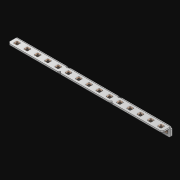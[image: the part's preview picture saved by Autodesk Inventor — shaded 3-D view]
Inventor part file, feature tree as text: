
AUTODESK INVENTOR PART (.ipt)
format: ipt  version: 2021 (Build 250183000, 183)  size: 669,696 bytes
history: native  units: in
note: dims shown in document units (in); Inventor stores cm internally (conversion verified against a paired STEP export)
features: extrude x31, other x30, sketch x3, pattern_linear x1, sheet_metal_op x1
ambient origin geometry x8: Origin, YZ Plane, XZ Plane, XY Plane, X Axis, Y Axis, Z Axis, Center Point
bodies: Solid1 (feature_tree)
feature tree (66):
  pattern_linear  "Rectangular Pattern1"  Spacing1=0.063in  [1 undecoded]
  extrude  "Extrusion1"  Depth=0.5in
  sketch  "Sketch1"  dims[d0=0.182in]
  other  "Srf1"
  sketch  "Sketch2"  dims[d1=0.063in d2=0.0in]
  other  "Srf2"
  other  "Srf3"
  other  "Srf5"
  other  "Srf7"
  other  "Srf9"
  other  "Srf11"
  other  "Srf13"
  other  "Srf15"
  other  "Srf17"
  other  "Srf19"
  other  "Srf21"
  other  "Srf23"
  other  "Srf25"
  other  "Srf27"
  other  "Srf29"
  other  "Srf4"
  other  "Srf6"
  other  "Srf8"
  other  "Srf10"
  other  "Srf12"
  other  "Srf14"
  other  "Srf16"
  other  "Srf18"
  other  "Srf20"
  other  "Srf22"
  other  "Srf24"
  other  "Srf26"
  other  "Srf28"
  other  "Srf30"
  sketch  "Sketch3"  dims[d3=0.182in d4=0.063in d5=0.0in d8=0.5in d9=10.0in d10=0.0in]
  sheet_metal_op  "Fold1"
  extrude  "ExtrusionSrf1"  Depth=0.5in TaperAngle=0.0deg
  extrude  "ExtrusionSrf2"  [1 undecoded]
  extrude  "ExtrusionSrf3"  [1 undecoded]
  extrude  "ExtrusionSrf4"  [1 undecoded]
  extrude  "ExtrusionSrf5"  [1 undecoded]
  extrude  "ExtrusionSrf6"  [1 undecoded]
  extrude  "ExtrusionSrf7"  [1 undecoded]
  extrude  "ExtrusionSrf8"  [1 undecoded]
  extrude  "ExtrusionSrf9"  [1 undecoded]
  extrude  "ExtrusionSrf10"  [1 undecoded]
  extrude  "ExtrusionSrf11"  [1 undecoded]
  extrude  "ExtrusionSrf12"  [1 undecoded]
  extrude  "ExtrusionSrf13"  [1 undecoded]
  extrude  "ExtrusionSrf14"  [1 undecoded]
  extrude  "ExtrusionSrf15"  [1 undecoded]
  extrude  "ExtrusionSrf16"  [1 undecoded]
  extrude  "ExtrusionSrf37"  [1 undecoded]
  extrude  "ExtrusionSrf38"  [1 undecoded]
  extrude  "ExtrusionSrf39"  [1 undecoded]
  extrude  "ExtrusionSrf40"  [1 undecoded]
  extrude  "ExtrusionSrf41"  [1 undecoded]
  extrude  "ExtrusionSrf42"  [1 undecoded]
  extrude  "ExtrusionSrf43"  [1 undecoded]
  extrude  "ExtrusionSrf44"  [1 undecoded]
  extrude  "ExtrusionSrf45"  [1 undecoded]
  extrude  "ExtrusionSrf46"  [1 undecoded]
  extrude  "ExtrusionSrf47"  [1 undecoded]
  extrude  "ExtrusionSrf48"  [1 undecoded]
  extrude  "ExtrusionSrf49"  [1 undecoded]
  extrude  "ExtrusionSrf50"  [1 undecoded]
note: 30 required parameter values undecoded (feature->parameter linkage not recoverable at this tier; creation-order binding heuristic only, values carry confidence <= 0.55)
